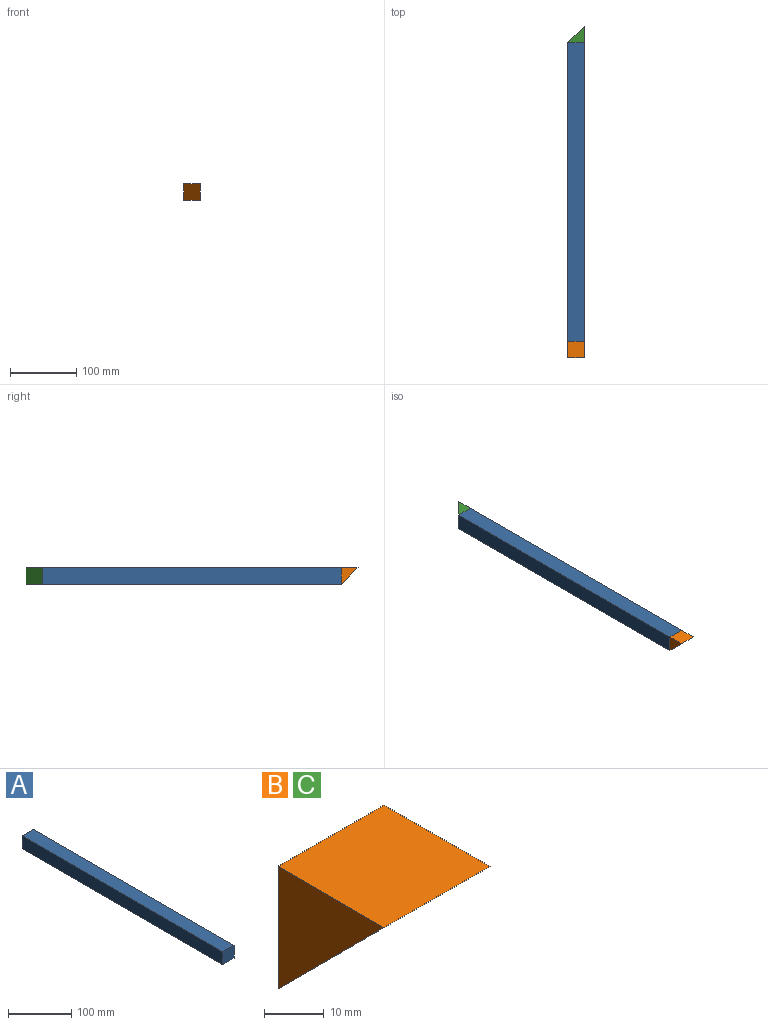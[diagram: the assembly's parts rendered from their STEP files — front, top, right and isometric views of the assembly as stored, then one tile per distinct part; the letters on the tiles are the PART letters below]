
ASSEMBLY  parts=3 mates=2
PART A: 6 faces, bbox 25x450x25 mm
  f0: plane 450x25mm, normal (0,0,1), area 11250mm2, adj f1,f3,f4,f5
  f1: plane 450x25mm, normal (-1,0,0), area 11250mm2, adj f0,f2,f4,f5
  f2: plane 450x25mm, normal (0,0,-1), area 11250mm2, adj f1,f3,f4,f5
  f3: plane 450x25mm, normal (1,0,0), area 11250mm2, adj f0,f2,f4,f5
  f4: plane 25x25mm, normal (0,-1,0), area 625mm2, adj f0,f1,f2,f3
  f5: plane 25x25mm, normal (0,1,0), area 625mm2, adj f0,f1,f2,f3
PART B: 5 faces, bbox 25x25x25 mm
  f0: plane 25x25mm, normal (-1,0,0), area 312.5mm2, adj f2,f3,f4
  f1: plane 25x25mm, normal (1,0,0), area 312.5mm2, adj f2,f3,f4
  f2: plane 25x25mm, normal (0,0,1), area 625mm2, adj f0,f1,f3,f4
  f3: plane 25x25mm, normal (0,1,0), area 625mm2, adj f0,f1,f2,f4
  f4: plane 25x25mm, normal (0,-0.71,-0.71), area 883.9mm2, adj f0,f1,f2,f3
PART C: same geometry as B
PLACE A t=(-137.4,116.7,-80.96)mm
PLACE B t=(-137.4,-333.3,-80.96)mm
PLACE C rot(axis=(0.71,0,0.71),180deg) t=(-137.4,116.7,-80.96)mm
MATE fastened C.f3 <-> A.f5  axis (0,-1,0) through (-137.4,116.7,-80.96)mm
MATE fastened B.f3 <-> A.f4  axis (0,1,0) through (-137.4,-333.3,-80.96)mm
